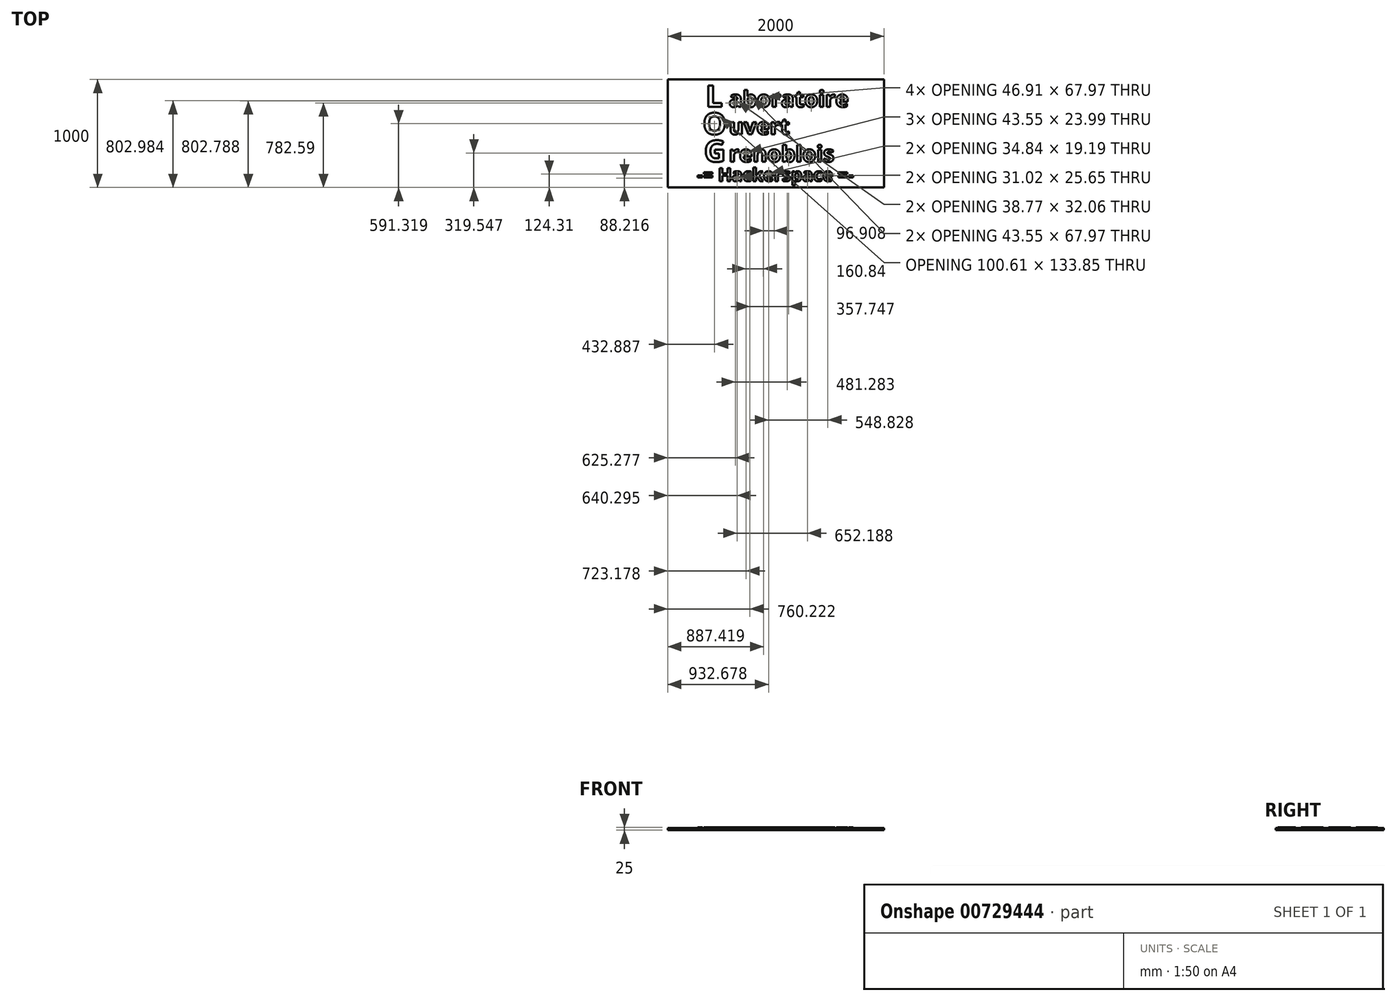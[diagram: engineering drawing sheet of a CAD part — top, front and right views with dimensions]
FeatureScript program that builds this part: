
annotation { "Feature Type Name" : "Feature", "Feature Type Description" : "" }
export const myFeature = defineFeature(function(context is Context, id is Id, definition is map)
    precondition{}
    {
        {
            var Q0;
            Q0=qCreatedBy(makeId("Top.planeOp"),FACE);
            var sketch = newSketch(context, id + "F0", { "sketchPlane" : qUnion([Q0])});
            skText(sketch, "E0", { "text": "aboratoire\n", "fontName": "OpenSans-Bold.ttf"});
            skText(sketch, "E1", { "text": "uvert", "fontName": "OpenSans-Bold.ttf"});
            skText(sketch, "E2", { "text": "renoblois", "fontName": "OpenSans-Bold.ttf"});
            skLineSegment(sketch, "E3", {"start": v(565.3, 745.92) * mm, "end": v(565.3, 641.84) * mm, "construction": true});
            skLineSegment(sketch, "E4", {"start": v(565.3, 491.84) * mm, "end": v(565.3, 387.76) * mm, "construction": true});
            skLineSegment(sketch, "E5.bottom", {"start": v(0, 1000) * mm, "end": v(2000, 1000) * mm});
            skLineSegment(sketch, "E5.top", {"start": v(0, 0) * mm, "end": v(2000, 0) * mm});
            skLineSegment(sketch, "E5.left", {"start": v(0, 1000) * mm, "end": v(0, 0) * mm});
            skLineSegment(sketch, "E5.right", {"start": v(2000, 1000) * mm, "end": v(2000, 0) * mm});
            skLineSegment(sketch, "E6", {"start": v(565.3, 895.92) * mm, "end": v(565.3, 1000) * mm, "construction": true});
            skText(sketch, "E7", { "text": "L", "fontName": "OpenSans-Bold.ttf"});
            skText(sketch, "E8", { "text": "O", "fontName": "OpenSans-Bold.ttf"});
            skText(sketch, "E9", { "text": "G", "fontName": "OpenSans-Bold.ttf"});
            skLineSegment(sketch, "E10", {"start": v(433.82, 745.92) * mm, "end": v(433.82, 691.84) * mm, "construction": true});
            skLineSegment(sketch, "E11", {"start": v(433.82, 491.84) * mm, "end": v(433.82, 437.76) * mm, "construction": true});
            skLineSegment(sketch, "E12", {"start": v(433.82, 945.92) * mm, "end": v(433.82, 1000) * mm, "construction": true});
            skLineSegment(sketch, "E13", {"start": v(322.34, 691.84) * mm, "end": v(0, 691.84) * mm, "construction": true});
            skLineSegment(sketch, "E14", {"start": v(545.3, 691.84) * mm, "end": v(565.3, 691.84) * mm, "construction": true});
            skLineSegment(sketch, "E15", {"start": v(1677.66, 895.92) * mm, "end": v(2000, 895.92) * mm, "construction": true});
            skText(sketch, "E16", { "text": "-= Hackerspace =-", "fontName": "OpenSans-Bold.ttf"});
            skLineSegment(sketch, "E17", {"start": v(272.73, 178.88) * mm, "end": v(0, 178.88) * mm, "construction": true});
            skLineSegment(sketch, "E18", {"start": v(1727.27, 178.88) * mm, "end": v(2000, 178.88) * mm, "construction": true});
            skLineSegment(sketch, "E19", {"start": v(565.3, 237.76) * mm, "end": v(565.3, 178.88) * mm, "construction": true});
            skLineSegment(sketch, "E20", {"start": v(568.68, 58.88) * mm, "end": v(568.68, 0) * mm, "construction": true});
            const initialGuessF0  = {"E0": [0.5653, 0.74592, 1, 0, 0.15], "E1": [0.5653, 0.49184, 1, 0, 0.15], "E2": [0.5653, 0.23776, 1, 0, 0.15], "E7": [0.35109, 0.74592, 1, 0, 0.2], "E8": [0.32234, 0.49184, 1, 0, 0.2], "E9": [0.33536, 0.23776, 1, 0, 0.2], "E16": [0.27273, 0.05888, 1, 0, 0.12]};
            skSetInitialGuess(sketch, initialGuessF0);
            skSolve(sketch);
        }
        {
            var Q0;
            Q0=makeQuery(id+"F0.imprint","IMPRINT",FACE,{"disambiguationData":[TD([[makeQuery(id+"F0.imprint","IMPRINT",EDGE,{"derivedFrom":sQuery(id+"F0.wireOp",EDGE,"E0.sketch_text.stroke-0")}),1.0]])]});
            var Q1;
            Q1=makeQuery(id+"F0.imprint","IMPRINT",FACE,{"disambiguationData":[TD([[makeQuery(id+"F0.imprint","IMPRINT",EDGE,{"derivedFrom":sQuery(id+"F0.wireOp",EDGE,"E1.sketch_text.stroke-60")}),-1.0]])]});
            var Q2;
            Q2=makeQuery(id+"F0.imprint","IMPRINT",FACE,{"disambiguationData":[TD([[makeQuery(id+"F0.imprint","IMPRINT",EDGE,{"derivedFrom":sQuery(id+"F0.wireOp",EDGE,"E1.sketch_text.stroke-27")}),1.0]])]});
            var Q3;
            Q3=makeQuery(id+"F0.imprint","IMPRINT",FACE,{"disambiguationData":[TD([[makeQuery(id+"F0.imprint","IMPRINT",EDGE,{"derivedFrom":sQuery(id+"F0.wireOp",EDGE,"E1.sketch_text.stroke-47")}),-1.0]])]});
            var Q4;
            Q4=makeQuery(id+"F0.imprint","IMPRINT",FACE,{"disambiguationData":[TD([[makeQuery(id+"F0.imprint","IMPRINT",EDGE,{"derivedFrom":sQuery(id+"F0.wireOp",EDGE,"E0.sketch_text.stroke-18")}),1.0]])]});
            var Q5;
            Q5=makeQuery(id+"F0.imprint","IMPRINT",FACE,{"disambiguationData":[TD([[makeQuery(id+"F0.imprint","IMPRINT",EDGE,{"derivedFrom":sQuery(id+"F0.wireOp",EDGE,"E0.sketch_text.stroke-39")}),1.0]])]});
            var Q6;
            Q6=makeQuery(id+"F0.imprint","IMPRINT",FACE,{"disambiguationData":[TD([[makeQuery(id+"F0.imprint","IMPRINT",EDGE,{"derivedFrom":sQuery(id+"F0.wireOp",EDGE,"E0.sketch_text.stroke-48")}),1.0]])]});
            var Q7;
            Q7=makeQuery(id+"F0.imprint","IMPRINT",FACE,{"disambiguationData":[TD([[makeQuery(id+"F0.imprint","IMPRINT",EDGE,{"derivedFrom":sQuery(id+"F0.wireOp",EDGE,"E0.sketch_text.stroke-66")}),-1.0]])]});
            var Q8;
            Q8=makeQuery(id+"F0.imprint","IMPRINT",FACE,{"disambiguationData":[TD([[makeQuery(id+"F0.imprint","IMPRINT",EDGE,{"derivedFrom":sQuery(id+"F0.wireOp",EDGE,"E0.sketch_text.stroke-97")}),1.0]])]});
            var Q9;
            Q9=makeQuery(id+"F0.imprint","IMPRINT",FACE,{"disambiguationData":[TD([[makeQuery(id+"F0.imprint","IMPRINT",EDGE,{"derivedFrom":sQuery(id+"F0.wireOp",EDGE,"E0.sketch_text.stroke-104")}),-1.0]])]});
            var Q10;
            Q10=makeQuery(id+"F0.imprint","IMPRINT",FACE,{"disambiguationData":[TD([[makeQuery(id+"F0.imprint","IMPRINT",EDGE,{"derivedFrom":sQuery(id+"F0.wireOp",EDGE,"E0.sketch_text.stroke-122")}),1.0]])]});
            var Q11;
            Q11=makeQuery(id+"F0.imprint","IMPRINT",FACE,{"disambiguationData":[TD([[makeQuery(id+"F0.imprint","IMPRINT",EDGE,{"derivedFrom":sQuery(id+"F0.wireOp",EDGE,"E0.sketch_text.stroke-140")}),-1.0]])]});
            var Q12;
            Q12=makeQuery(id+"F0.imprint","IMPRINT",FACE,{"disambiguationData":[TD([[makeQuery(id+"F0.imprint","IMPRINT",EDGE,{"derivedFrom":sQuery(id+"F0.wireOp",EDGE,"E0.sketch_text.stroke-145")}),-1.0]])]});
            var Q13;
            Q13=makeQuery(id+"F0.imprint","IMPRINT",FACE,{"disambiguationData":[TD([[makeQuery(id+"F0.imprint","IMPRINT",EDGE,{"derivedFrom":sQuery(id+"F0.wireOp",EDGE,"E0.sketch_text.stroke-149")}),-1.0]])]});
            var Q14;
            Q14=makeQuery(id+"F0.imprint","IMPRINT",FACE,{"disambiguationData":[TD([[makeQuery(id+"F0.imprint","IMPRINT",EDGE,{"derivedFrom":sQuery(id+"F0.wireOp",EDGE,"E0.sketch_text.stroke-162")}),1.0]])]});
            var Q15;
            Q15=makeQuery(id+"F0.imprint","IMPRINT",FACE,{"disambiguationData":[TD([[makeQuery(id+"F0.imprint","IMPRINT",EDGE,{"derivedFrom":sQuery(id+"F0.wireOp",EDGE,"E1.sketch_text.stroke-0")}),-1.0]])]});
            var Q16;
            Q16=makeQuery(id+"F0.imprint","IMPRINT",FACE,{"disambiguationData":[TD([[makeQuery(id+"F0.imprint","IMPRINT",EDGE,{"derivedFrom":sQuery(id+"F0.wireOp",EDGE,"E1.sketch_text.stroke-17")}),-1.0]])]});
            var Q17;
            Q17=makeQuery(id+"F0.imprint","IMPRINT",FACE,{"disambiguationData":[TD([[makeQuery(id+"F0.imprint","IMPRINT",EDGE,{"derivedFrom":sQuery(id+"F0.wireOp",EDGE,"E16.sketch_text.stroke-8")}),-1.0]])]});
            var Q18;
            Q18=makeQuery(id+"F0.imprint","IMPRINT",FACE,{"disambiguationData":[TD([[makeQuery(id+"F0.imprint","IMPRINT",EDGE,{"derivedFrom":sQuery(id+"F0.wireOp",EDGE,"E0.sketch_text.stroke-25")}),-1.0]])]});
            var Q19;
            Q19=makeQuery(id+"F0.imprint","IMPRINT",FACE,{"disambiguationData":[TD([[makeQuery(id+"F0.imprint","IMPRINT",EDGE,{"derivedFrom":sQuery(id+"F0.wireOp",EDGE,"E16.sketch_text.stroke-160")}),-1.0]])]});
            var Q20;
            Q20=makeQuery(id+"F0.imprint","IMPRINT",FACE,{"disambiguationData":[TD([[makeQuery(id+"F0.imprint","IMPRINT",EDGE,{"derivedFrom":sQuery(id+"F0.wireOp",EDGE,"E16.sketch_text.stroke-227")}),-1.0]])]});
            var Q21;
            Q21=makeQuery(id+"F0.imprint","IMPRINT",FACE,{"disambiguationData":[TD([[makeQuery(id+"F0.imprint","IMPRINT",EDGE,{"derivedFrom":sQuery(id+"F0.wireOp",EDGE,"E16.sketch_text.stroke-0")}),-1.0]])]});
            var Q22;
            Q22=makeQuery(id+"F0.imprint","IMPRINT",FACE,{"disambiguationData":[TD([[makeQuery(id+"F0.imprint","IMPRINT",EDGE,{"derivedFrom":sQuery(id+"F0.wireOp",EDGE,"E16.sketch_text.stroke-199")}),-1.0]])]});
            var Q23;
            Q23=makeQuery(id+"F0.imprint","IMPRINT",FACE,{"disambiguationData":[TD([[makeQuery(id+"F0.imprint","IMPRINT",EDGE,{"derivedFrom":sQuery(id+"F0.wireOp",EDGE,"E0.sketch_text.stroke-0")}),-1.0]])]});
            var Q24;
            Q24=makeQuery(id+"F0.imprint","IMPRINT",FACE,{"disambiguationData":[TD([[makeQuery(id+"F0.imprint","IMPRINT",EDGE,{"derivedFrom":sQuery(id+"F0.wireOp",EDGE,"E2.sketch_text.stroke-0")}),-1.0]])]});
            var Q25;
            Q25=makeQuery(id+"F0.imprint","IMPRINT",FACE,{"disambiguationData":[TD([[makeQuery(id+"F0.imprint","IMPRINT",EDGE,{"derivedFrom":sQuery(id+"F0.wireOp",EDGE,"E0.sketch_text.stroke-48")}),-1.0]])]});
            var Q26;
            Q26=makeQuery(id+"F0.imprint","IMPRINT",FACE,{"disambiguationData":[TD([[makeQuery(id+"F0.imprint","IMPRINT",EDGE,{"derivedFrom":sQuery(id+"F0.wireOp",EDGE,"E16.sketch_text.stroke-12")}),-1.0]])]});
            var Q27;
            Q27=makeQuery(id+"F0.imprint","IMPRINT",FACE,{"disambiguationData":[TD([[makeQuery(id+"F0.imprint","IMPRINT",EDGE,{"derivedFrom":sQuery(id+"F0.wireOp",EDGE,"E2.sketch_text.stroke-13")}),1.0]])]});
            var Q28;
            Q28=makeQuery(id+"F0.imprint","IMPRINT",FACE,{"disambiguationData":[TD([[makeQuery(id+"F0.imprint","IMPRINT",EDGE,{"derivedFrom":sQuery(id+"F0.wireOp",EDGE,"E0.sketch_text.stroke-79")}),-1.0]])]});
            var Q29;
            Q29=makeQuery(id+"F0.imprint","IMPRINT",FACE,{"disambiguationData":[TD([[makeQuery(id+"F0.imprint","IMPRINT",EDGE,{"derivedFrom":sQuery(id+"F0.wireOp",EDGE,"E2.sketch_text.stroke-33")}),-1.0]])]});
            var Q30;
            Q30=makeQuery(id+"F0.imprint","IMPRINT",FACE,{"disambiguationData":[TD([[makeQuery(id+"F0.imprint","IMPRINT",EDGE,{"derivedFrom":sQuery(id+"F0.wireOp",EDGE,"E0.sketch_text.stroke-122")}),-1.0]])]});
            var Q31;
            Q31=makeQuery(id+"F0.imprint","IMPRINT",FACE,{"disambiguationData":[TD([[makeQuery(id+"F0.imprint","IMPRINT",EDGE,{"derivedFrom":sQuery(id+"F0.wireOp",EDGE,"E16.sketch_text.stroke-49")}),-1.0]])]});
            var Q32;
            Q32=makeQuery(id+"F0.imprint","IMPRINT",FACE,{"disambiguationData":[TD([[makeQuery(id+"F0.imprint","IMPRINT",EDGE,{"derivedFrom":sQuery(id+"F0.wireOp",EDGE,"E2.sketch_text.stroke-50")}),1.0]])]});
            var Q33;
            Q33=makeQuery(id+"F0.imprint","IMPRINT",FACE,{"disambiguationData":[TD([[makeQuery(id+"F0.imprint","IMPRINT",EDGE,{"derivedFrom":sQuery(id+"F0.wireOp",EDGE,"E0.sketch_text.stroke-162")}),-1.0]])]});
            var Q34;
            Q34=makeQuery(id+"F0.imprint","IMPRINT",FACE,{"disambiguationData":[TD([[makeQuery(id+"F0.imprint","IMPRINT",EDGE,{"derivedFrom":sQuery(id+"F0.wireOp",EDGE,"E16.sketch_text.stroke-63")}),-1.0]])]});
            var Q35;
            Q35=makeQuery(id+"F0.imprint","IMPRINT",FACE,{"disambiguationData":[TD([[makeQuery(id+"F0.imprint","IMPRINT",EDGE,{"derivedFrom":sQuery(id+"F0.wireOp",EDGE,"E2.sketch_text.stroke-82")}),1.0]])]});
            var Q36;
            Q36=makeQuery(id+"F0.imprint","IMPRINT",FACE,{"disambiguationData":[TD([[makeQuery(id+"F0.imprint","IMPRINT",EDGE,{"derivedFrom":sQuery(id+"F0.wireOp",EDGE,"E1.sketch_text.stroke-27")}),-1.0]])]});
            var Q37;
            Q37=makeQuery(id+"F0.imprint","IMPRINT",FACE,{"disambiguationData":[TD([[makeQuery(id+"F0.imprint","IMPRINT",EDGE,{"derivedFrom":sQuery(id+"F0.wireOp",EDGE,"E2.sketch_text.stroke-91")}),-1.0]])]});
            var Q38;
            Q38=makeQuery(id+"F0.imprint","IMPRINT",FACE,{"disambiguationData":[TD([[makeQuery(id+"F0.imprint","IMPRINT",EDGE,{"derivedFrom":sQuery(id+"F0.wireOp",EDGE,"E2.sketch_text.stroke-13")}),-1.0]])]});
            var Q39;
            Q39=makeQuery(id+"F0.imprint","IMPRINT",FACE,{"disambiguationData":[TD([[makeQuery(id+"F0.imprint","IMPRINT",EDGE,{"derivedFrom":sQuery(id+"F0.wireOp",EDGE,"E16.sketch_text.stroke-98")}),-1.0]])]});
            var Q40;
            Q40=makeQuery(id+"F0.imprint","IMPRINT",FACE,{"disambiguationData":[TD([[makeQuery(id+"F0.imprint","IMPRINT",EDGE,{"derivedFrom":sQuery(id+"F0.wireOp",EDGE,"E2.sketch_text.stroke-50")}),-1.0]])]});
            var Q41;
            Q41=makeQuery(id+"F0.imprint","IMPRINT",FACE,{"disambiguationData":[TD([[makeQuery(id+"F0.imprint","IMPRINT",EDGE,{"derivedFrom":sQuery(id+"F0.wireOp",EDGE,"E16.sketch_text.stroke-111")}),-1.0]])]});
            var Q42;
            Q42=makeQuery(id+"F0.imprint","IMPRINT",FACE,{"disambiguationData":[TD([[makeQuery(id+"F0.imprint","IMPRINT",EDGE,{"derivedFrom":sQuery(id+"F0.wireOp",EDGE,"E2.sketch_text.stroke-95")}),1.0]])]});
            var Q43;
            Q43=makeQuery(id+"F0.imprint","IMPRINT",FACE,{"disambiguationData":[TD([[makeQuery(id+"F0.imprint","IMPRINT",EDGE,{"derivedFrom":sQuery(id+"F0.wireOp",EDGE,"E2.sketch_text.stroke-68")}),-1.0]])]});
            var Q44;
            Q44=makeQuery(id+"F0.imprint","IMPRINT",FACE,{"disambiguationData":[TD([[makeQuery(id+"F0.imprint","IMPRINT",EDGE,{"derivedFrom":sQuery(id+"F0.wireOp",EDGE,"E16.sketch_text.stroke-152")}),1.0]])]});
            var Q45;
            Q45=makeQuery(id+"F0.imprint","IMPRINT",FACE,{"disambiguationData":[TD([[makeQuery(id+"F0.imprint","IMPRINT",EDGE,{"derivedFrom":sQuery(id+"F0.wireOp",EDGE,"E2.sketch_text.stroke-113")}),-1.0]])]});
            var Q46;
            Q46=makeQuery(id+"F0.imprint","IMPRINT",FACE,{"disambiguationData":[TD([[makeQuery(id+"F0.imprint","IMPRINT",EDGE,{"derivedFrom":sQuery(id+"F0.wireOp",EDGE,"E2.sketch_text.stroke-95")}),-1.0]])]});
            var Q47;
            Q47=makeQuery(id+"F0.imprint","IMPRINT",FACE,{"disambiguationData":[TD([[makeQuery(id+"F0.imprint","IMPRINT",EDGE,{"derivedFrom":sQuery(id+"F0.wireOp",EDGE,"E16.sketch_text.stroke-178")}),1.0]])]});
            var Q48;
            Q48=makeQuery(id+"F0.imprint","IMPRINT",FACE,{"disambiguationData":[TD([[makeQuery(id+"F0.imprint","IMPRINT",EDGE,{"derivedFrom":sQuery(id+"F0.wireOp",EDGE,"E2.sketch_text.stroke-118")}),-1.0]])]});
            var Q49;
            Q49=makeQuery(id+"F0.imprint","IMPRINT",FACE,{"disambiguationData":[TD([[makeQuery(id+"F0.imprint","IMPRINT",EDGE,{"derivedFrom":sQuery(id+"F0.wireOp",EDGE,"E8.sketch_text.stroke-0")}),-1.0]])]});
            var Q50;
            Q50=makeQuery(id+"F0.imprint","IMPRINT",FACE,{"disambiguationData":[TD([[makeQuery(id+"F0.imprint","IMPRINT",EDGE,{"derivedFrom":sQuery(id+"F0.wireOp",EDGE,"E16.sketch_text.stroke-185")}),-1.0]])]});
            var Q51;
            Q51=makeQuery(id+"F0.imprint","IMPRINT",FACE,{"disambiguationData":[TD([[makeQuery(id+"F0.imprint","IMPRINT",EDGE,{"derivedFrom":sQuery(id+"F0.wireOp",EDGE,"E2.sketch_text.stroke-122")}),-1.0]])]});
            var Q52;
            Q52=makeQuery(id+"F0.imprint","IMPRINT",FACE,{"disambiguationData":[TD([[makeQuery(id+"F0.imprint","IMPRINT",EDGE,{"derivedFrom":sQuery(id+"F0.wireOp",EDGE,"E16.sketch_text.stroke-24")}),-1.0]])]});
            var Q53;
            Q53=makeQuery(id+"F0.imprint","IMPRINT",FACE,{"disambiguationData":[TD([[makeQuery(id+"F0.imprint","IMPRINT",EDGE,{"derivedFrom":sQuery(id+"F0.wireOp",EDGE,"E7.sketch_text.stroke-0")}),-1.0]])]});
            var Q54;
            Q54=makeQuery(id+"F0.imprint","IMPRINT",FACE,{"disambiguationData":[TD([[makeQuery(id+"F0.imprint","IMPRINT",EDGE,{"derivedFrom":sQuery(id+"F0.wireOp",EDGE,"E16.sketch_text.stroke-78")}),-1.0]])]});
            var Q55;
            Q55=makeQuery(id+"F0.imprint","IMPRINT",FACE,{"disambiguationData":[TD([[makeQuery(id+"F0.imprint","IMPRINT",EDGE,{"derivedFrom":sQuery(id+"F0.wireOp",EDGE,"E8.sketch_text.stroke-8")}),1.0]])]});
            var Q56;
            Q56=makeQuery(id+"F0.imprint","IMPRINT",FACE,{"disambiguationData":[TD([[makeQuery(id+"F0.imprint","IMPRINT",EDGE,{"derivedFrom":sQuery(id+"F0.wireOp",EDGE,"E16.sketch_text.stroke-137")}),-1.0]])]});
            var Q57;
            Q57=makeQuery(id+"F0.imprint","IMPRINT",FACE,{"disambiguationData":[TD([[makeQuery(id+"F0.imprint","IMPRINT",EDGE,{"derivedFrom":sQuery(id+"F0.wireOp",EDGE,"E16.sketch_text.stroke-223")}),-1.0]])]});
            var Q58;
            Q58=makeQuery(id+"F0.imprint","IMPRINT",FACE,{"disambiguationData":[TD([[makeQuery(id+"F0.imprint","IMPRINT",EDGE,{"derivedFrom":sQuery(id+"F0.wireOp",EDGE,"E9.sketch_text.stroke-0")}),-1.0]])]});
            var Q59;
            Q59=makeQuery(id+"F0.imprint","IMPRINT",FACE,{"disambiguationData":[TD([[makeQuery(id+"F0.imprint","IMPRINT",EDGE,{"derivedFrom":sQuery(id+"F0.wireOp",EDGE,"E16.sketch_text.stroke-4")}),-1.0]])]});
            var Q60;
            Q60=makeQuery(id+"F0.imprint","IMPRINT",FACE,{"disambiguationData":[TD([[makeQuery(id+"F0.imprint","IMPRINT",EDGE,{"derivedFrom":sQuery(id+"F0.wireOp",EDGE,"E16.sketch_text.stroke-42")}),1.0]])]});
            var Q61;
            Q61=makeQuery(id+"F0.imprint","IMPRINT",FACE,{"disambiguationData":[TD([[makeQuery(id+"F0.imprint","IMPRINT",EDGE,{"derivedFrom":sQuery(id+"F0.wireOp",EDGE,"E16.sketch_text.stroke-78")}),1.0]])]});
            var Q62;
            Q62=makeQuery(id+"F0.imprint","IMPRINT",FACE,{"disambiguationData":[TD([[makeQuery(id+"F0.imprint","IMPRINT",EDGE,{"derivedFrom":sQuery(id+"F0.wireOp",EDGE,"E16.sketch_text.stroke-199")}),1.0]])]});
            var Q63;
            Q63=makeQuery(id+"F0.imprint","IMPRINT",FACE,{"disambiguationData":[TD([[makeQuery(id+"F0.imprint","IMPRINT",EDGE,{"derivedFrom":sQuery(id+"F0.wireOp",EDGE,"E16.sketch_text.stroke-219")}),-1.0]])]});
            extrude(context, id + "F1", {"entities" : qUnion([Q0, Q1, Q2, Q3, Q4, Q5, Q6, Q7, Q8, Q9, Q10, Q11, Q12, Q13, Q14, Q15, Q16, Q17, Q18, Q19, Q20, Q21, Q22, Q23, Q24, Q25, Q26, Q27, Q28, Q29, Q30, Q31, Q32, Q33, Q34, Q35, Q36, Q37, Q38, Q39, Q40, Q41, Q42, Q43, Q44, Q45, Q46, Q47, Q48, Q49, Q50, Q51, Q52, Q53, Q54, Q55, Q56, Q57, Q58, Q59, Q60, Q61, Q62, Q63]), "oppositeDirection" : true, "depth" : 20 * mm, "offsetDistance" : 25 * mm});
        }
        {
            var Q0;
            Q0=makeQuery(id+"F0.imprint","IMPRINT",FACE,{"disambiguationData":[TD([[makeQuery(id+"F0.imprint","IMPRINT",EDGE,{"derivedFrom":sQuery(id+"F0.wireOp",EDGE,"E0.sketch_text.stroke-0")}),-1.0]])]});
            var Q1;
            Q1=makeQuery(id+"F0.imprint","IMPRINT",FACE,{"disambiguationData":[TD([[makeQuery(id+"F0.imprint","IMPRINT",EDGE,{"derivedFrom":sQuery(id+"F0.wireOp",EDGE,"E1.sketch_text.stroke-0")}),-1.0]])]});
            var Q2;
            Q2=makeQuery(id+"F0.imprint","IMPRINT",FACE,{"disambiguationData":[TD([[makeQuery(id+"F0.imprint","IMPRINT",EDGE,{"derivedFrom":sQuery(id+"F0.wireOp",EDGE,"E2.sketch_text.stroke-0")}),-1.0]])]});
            var Q3;
            Q3=makeQuery(id+"F0.imprint","IMPRINT",FACE,{"disambiguationData":[TD([[makeQuery(id+"F0.imprint","IMPRINT",EDGE,{"derivedFrom":sQuery(id+"F0.wireOp",EDGE,"E0.sketch_text.stroke-25")}),-1.0]])]});
            var Q4;
            Q4=makeQuery(id+"F0.imprint","IMPRINT",FACE,{"disambiguationData":[TD([[makeQuery(id+"F0.imprint","IMPRINT",EDGE,{"derivedFrom":sQuery(id+"F0.wireOp",EDGE,"E0.sketch_text.stroke-48")}),-1.0]])]});
            var Q5;
            Q5=makeQuery(id+"F0.imprint","IMPRINT",FACE,{"disambiguationData":[TD([[makeQuery(id+"F0.imprint","IMPRINT",EDGE,{"derivedFrom":sQuery(id+"F0.wireOp",EDGE,"E0.sketch_text.stroke-66")}),-1.0]])]});
            var Q6;
            Q6=makeQuery(id+"F0.imprint","IMPRINT",FACE,{"disambiguationData":[TD([[makeQuery(id+"F0.imprint","IMPRINT",EDGE,{"derivedFrom":sQuery(id+"F0.wireOp",EDGE,"E0.sketch_text.stroke-79")}),-1.0]])]});
            var Q7;
            Q7=makeQuery(id+"F0.imprint","IMPRINT",FACE,{"disambiguationData":[TD([[makeQuery(id+"F0.imprint","IMPRINT",EDGE,{"derivedFrom":sQuery(id+"F0.wireOp",EDGE,"E0.sketch_text.stroke-104")}),-1.0]])]});
            var Q8;
            Q8=makeQuery(id+"F0.imprint","IMPRINT",FACE,{"disambiguationData":[TD([[makeQuery(id+"F0.imprint","IMPRINT",EDGE,{"derivedFrom":sQuery(id+"F0.wireOp",EDGE,"E0.sketch_text.stroke-122")}),-1.0]])]});
            var Q9;
            Q9=makeQuery(id+"F0.imprint","IMPRINT",FACE,{"disambiguationData":[TD([[makeQuery(id+"F0.imprint","IMPRINT",EDGE,{"derivedFrom":sQuery(id+"F0.wireOp",EDGE,"E0.sketch_text.stroke-149")}),-1.0]])]});
            var Q10;
            Q10=makeQuery(id+"F0.imprint","IMPRINT",FACE,{"disambiguationData":[TD([[makeQuery(id+"F0.imprint","IMPRINT",EDGE,{"derivedFrom":sQuery(id+"F0.wireOp",EDGE,"E0.sketch_text.stroke-145")}),-1.0]])]});
            var Q11;
            Q11=makeQuery(id+"F0.imprint","IMPRINT",FACE,{"disambiguationData":[TD([[makeQuery(id+"F0.imprint","IMPRINT",EDGE,{"derivedFrom":sQuery(id+"F0.wireOp",EDGE,"E0.sketch_text.stroke-162")}),-1.0]])]});
            var Q12;
            Q12=makeQuery(id+"F0.imprint","IMPRINT",FACE,{"disambiguationData":[TD([[makeQuery(id+"F0.imprint","IMPRINT",EDGE,{"derivedFrom":sQuery(id+"F0.wireOp",EDGE,"E1.sketch_text.stroke-60")}),-1.0]])]});
            var Q13;
            Q13=makeQuery(id+"F0.imprint","IMPRINT",FACE,{"disambiguationData":[TD([[makeQuery(id+"F0.imprint","IMPRINT",EDGE,{"derivedFrom":sQuery(id+"F0.wireOp",EDGE,"E1.sketch_text.stroke-27")}),-1.0]])]});
            var Q14;
            Q14=makeQuery(id+"F0.imprint","IMPRINT",FACE,{"disambiguationData":[TD([[makeQuery(id+"F0.imprint","IMPRINT",EDGE,{"derivedFrom":sQuery(id+"F0.wireOp",EDGE,"E2.sketch_text.stroke-13")}),-1.0]])]});
            var Q15;
            Q15=makeQuery(id+"F0.imprint","IMPRINT",FACE,{"disambiguationData":[TD([[makeQuery(id+"F0.imprint","IMPRINT",EDGE,{"derivedFrom":sQuery(id+"F0.wireOp",EDGE,"E2.sketch_text.stroke-50")}),-1.0]])]});
            var Q16;
            Q16=makeQuery(id+"F0.imprint","IMPRINT",FACE,{"disambiguationData":[TD([[makeQuery(id+"F0.imprint","IMPRINT",EDGE,{"derivedFrom":sQuery(id+"F0.wireOp",EDGE,"E2.sketch_text.stroke-68")}),-1.0]])]});
            var Q17;
            Q17=makeQuery(id+"F0.imprint","IMPRINT",FACE,{"disambiguationData":[TD([[makeQuery(id+"F0.imprint","IMPRINT",EDGE,{"derivedFrom":sQuery(id+"F0.wireOp",EDGE,"E2.sketch_text.stroke-95")}),-1.0]])]});
            var Q18;
            Q18=makeQuery(id+"F0.imprint","IMPRINT",FACE,{"disambiguationData":[TD([[makeQuery(id+"F0.imprint","IMPRINT",EDGE,{"derivedFrom":sQuery(id+"F0.wireOp",EDGE,"E2.sketch_text.stroke-113")}),-1.0]])]});
            var Q19;
            Q19=makeQuery(id+"F0.imprint","IMPRINT",FACE,{"disambiguationData":[TD([[makeQuery(id+"F0.imprint","IMPRINT",EDGE,{"derivedFrom":sQuery(id+"F0.wireOp",EDGE,"E2.sketch_text.stroke-122")}),-1.0]])]});
            var Q20;
            Q20=makeQuery(id+"F0.imprint","IMPRINT",FACE,{"disambiguationData":[TD([[makeQuery(id+"F0.imprint","IMPRINT",EDGE,{"derivedFrom":sQuery(id+"F0.wireOp",EDGE,"E1.sketch_text.stroke-17")}),-1.0]])]});
            var Q21;
            Q21=makeQuery(id+"F0.imprint","IMPRINT",FACE,{"disambiguationData":[TD([[makeQuery(id+"F0.imprint","IMPRINT",EDGE,{"derivedFrom":sQuery(id+"F0.wireOp",EDGE,"E1.sketch_text.stroke-47")}),-1.0]])]});
            var Q22;
            Q22=makeQuery(id+"F0.imprint","IMPRINT",FACE,{"disambiguationData":[TD([[makeQuery(id+"F0.imprint","IMPRINT",EDGE,{"derivedFrom":sQuery(id+"F0.wireOp",EDGE,"E2.sketch_text.stroke-33")}),-1.0]])]});
            var Q23;
            Q23=makeQuery(id+"F0.imprint","IMPRINT",FACE,{"disambiguationData":[TD([[makeQuery(id+"F0.imprint","IMPRINT",EDGE,{"derivedFrom":sQuery(id+"F0.wireOp",EDGE,"E2.sketch_text.stroke-91")}),-1.0]])]});
            var Q24;
            Q24=makeQuery(id+"F0.imprint","IMPRINT",FACE,{"disambiguationData":[TD([[makeQuery(id+"F0.imprint","IMPRINT",EDGE,{"derivedFrom":sQuery(id+"F0.wireOp",EDGE,"E2.sketch_text.stroke-118")}),-1.0]])]});
            var Q25;
            Q25=makeQuery(id+"F0.imprint","IMPRINT",FACE,{"disambiguationData":[TD([[makeQuery(id+"F0.imprint","IMPRINT",EDGE,{"derivedFrom":sQuery(id+"F0.wireOp",EDGE,"E9.sketch_text.stroke-0")}),-1.0]])]});
            var Q26;
            Q26=makeQuery(id+"F0.imprint","IMPRINT",FACE,{"disambiguationData":[TD([[makeQuery(id+"F0.imprint","IMPRINT",EDGE,{"derivedFrom":sQuery(id+"F0.wireOp",EDGE,"E8.sketch_text.stroke-0")}),-1.0]])]});
            var Q27;
            Q27=makeQuery(id+"F0.imprint","IMPRINT",FACE,{"disambiguationData":[TD([[makeQuery(id+"F0.imprint","IMPRINT",EDGE,{"derivedFrom":sQuery(id+"F0.wireOp",EDGE,"E7.sketch_text.stroke-0")}),-1.0]])]});
            var Q28;
            Q28=makeQuery(id+"F0.imprint","IMPRINT",FACE,{"disambiguationData":[TD([[makeQuery(id+"F0.imprint","IMPRINT",EDGE,{"derivedFrom":sQuery(id+"F0.wireOp",EDGE,"E0.sketch_text.stroke-140")}),-1.0]])]});
            var Q29;
            Q29=makeQuery(id+"F0.imprint","IMPRINT",FACE,{"disambiguationData":[TD([[makeQuery(id+"F0.imprint","IMPRINT",EDGE,{"derivedFrom":sQuery(id+"F0.wireOp",EDGE,"E16.sketch_text.stroke-219")}),-1.0]])]});
            var Q30;
            Q30=makeQuery(id+"F0.imprint","IMPRINT",FACE,{"disambiguationData":[TD([[makeQuery(id+"F0.imprint","IMPRINT",EDGE,{"derivedFrom":sQuery(id+"F0.wireOp",EDGE,"E16.sketch_text.stroke-185")}),-1.0]])]});
            var Q31;
            Q31=makeQuery(id+"F0.imprint","IMPRINT",FACE,{"disambiguationData":[TD([[makeQuery(id+"F0.imprint","IMPRINT",EDGE,{"derivedFrom":sQuery(id+"F0.wireOp",EDGE,"E16.sketch_text.stroke-111")}),-1.0]])]});
            var Q32;
            Q32=makeQuery(id+"F0.imprint","IMPRINT",FACE,{"disambiguationData":[TD([[makeQuery(id+"F0.imprint","IMPRINT",EDGE,{"derivedFrom":sQuery(id+"F0.wireOp",EDGE,"E16.sketch_text.stroke-78")}),-1.0]])]});
            var Q33;
            Q33=makeQuery(id+"F0.imprint","IMPRINT",FACE,{"disambiguationData":[TD([[makeQuery(id+"F0.imprint","IMPRINT",EDGE,{"derivedFrom":sQuery(id+"F0.wireOp",EDGE,"E16.sketch_text.stroke-24")}),-1.0]])]});
            var Q34;
            Q34=makeQuery(id+"F0.imprint","IMPRINT",FACE,{"disambiguationData":[TD([[makeQuery(id+"F0.imprint","IMPRINT",EDGE,{"derivedFrom":sQuery(id+"F0.wireOp",EDGE,"E16.sketch_text.stroke-160")}),-1.0]])]});
            var Q35;
            Q35=makeQuery(id+"F0.imprint","IMPRINT",FACE,{"disambiguationData":[TD([[makeQuery(id+"F0.imprint","IMPRINT",EDGE,{"derivedFrom":sQuery(id+"F0.wireOp",EDGE,"E16.sketch_text.stroke-49")}),-1.0]])]});
            var Q36;
            Q36=makeQuery(id+"F0.imprint","IMPRINT",FACE,{"disambiguationData":[TD([[makeQuery(id+"F0.imprint","IMPRINT",EDGE,{"derivedFrom":sQuery(id+"F0.wireOp",EDGE,"E16.sketch_text.stroke-12")}),-1.0]])]});
            var Q37;
            Q37=makeQuery(id+"F0.imprint","IMPRINT",FACE,{"disambiguationData":[TD([[makeQuery(id+"F0.imprint","IMPRINT",EDGE,{"derivedFrom":sQuery(id+"F0.wireOp",EDGE,"E16.sketch_text.stroke-98")}),-1.0]])]});
            var Q38;
            Q38=makeQuery(id+"F0.imprint","IMPRINT",FACE,{"disambiguationData":[TD([[makeQuery(id+"F0.imprint","IMPRINT",EDGE,{"derivedFrom":sQuery(id+"F0.wireOp",EDGE,"E16.sketch_text.stroke-63")}),-1.0]])]});
            var Q39;
            Q39=makeQuery(id+"F0.imprint","IMPRINT",FACE,{"disambiguationData":[TD([[makeQuery(id+"F0.imprint","IMPRINT",EDGE,{"derivedFrom":sQuery(id+"F0.wireOp",EDGE,"E16.sketch_text.stroke-199")}),-1.0]])]});
            var Q40;
            Q40=makeQuery(id+"F0.imprint","IMPRINT",FACE,{"disambiguationData":[TD([[makeQuery(id+"F0.imprint","IMPRINT",EDGE,{"derivedFrom":sQuery(id+"F0.wireOp",EDGE,"E16.sketch_text.stroke-4")}),-1.0]])]});
            var Q41;
            Q41=makeQuery(id+"F0.imprint","IMPRINT",FACE,{"disambiguationData":[TD([[makeQuery(id+"F0.imprint","IMPRINT",EDGE,{"derivedFrom":sQuery(id+"F0.wireOp",EDGE,"E16.sketch_text.stroke-223")}),-1.0]])]});
            var Q42;
            Q42=makeQuery(id+"F0.imprint","IMPRINT",FACE,{"disambiguationData":[TD([[makeQuery(id+"F0.imprint","IMPRINT",EDGE,{"derivedFrom":sQuery(id+"F0.wireOp",EDGE,"E16.sketch_text.stroke-0")}),-1.0]])]});
            var Q43;
            Q43=makeQuery(id+"F0.imprint","IMPRINT",FACE,{"disambiguationData":[TD([[makeQuery(id+"F0.imprint","IMPRINT",EDGE,{"derivedFrom":sQuery(id+"F0.wireOp",EDGE,"E16.sketch_text.stroke-227")}),-1.0]])]});
            var Q44;
            Q44=makeQuery(id+"F0.imprint","IMPRINT",FACE,{"disambiguationData":[TD([[makeQuery(id+"F0.imprint","IMPRINT",EDGE,{"derivedFrom":sQuery(id+"F0.wireOp",EDGE,"E16.sketch_text.stroke-8")}),-1.0]])]});
            var Q45;
            Q45=makeQuery(id+"F0.imprint","IMPRINT",FACE,{"disambiguationData":[TD([[makeQuery(id+"F0.imprint","IMPRINT",EDGE,{"derivedFrom":sQuery(id+"F0.wireOp",EDGE,"E16.sketch_text.stroke-137")}),-1.0]])]});
            extrude(context, id + "F2", {"entities" : qUnion([Q0, Q1, Q2, Q3, Q4, Q5, Q6, Q7, Q8, Q9, Q10, Q11, Q12, Q13, Q14, Q15, Q16, Q17, Q18, Q19, Q20, Q21, Q22, Q23, Q24, Q25, Q26, Q27, Q28, Q29, Q30, Q31, Q32, Q33, Q34, Q35, Q36, Q37, Q38, Q39, Q40, Q41, Q42, Q43, Q44, Q45]), "depth" : 5 * mm, "offsetDistance" : 25 * mm});
        }
    });
